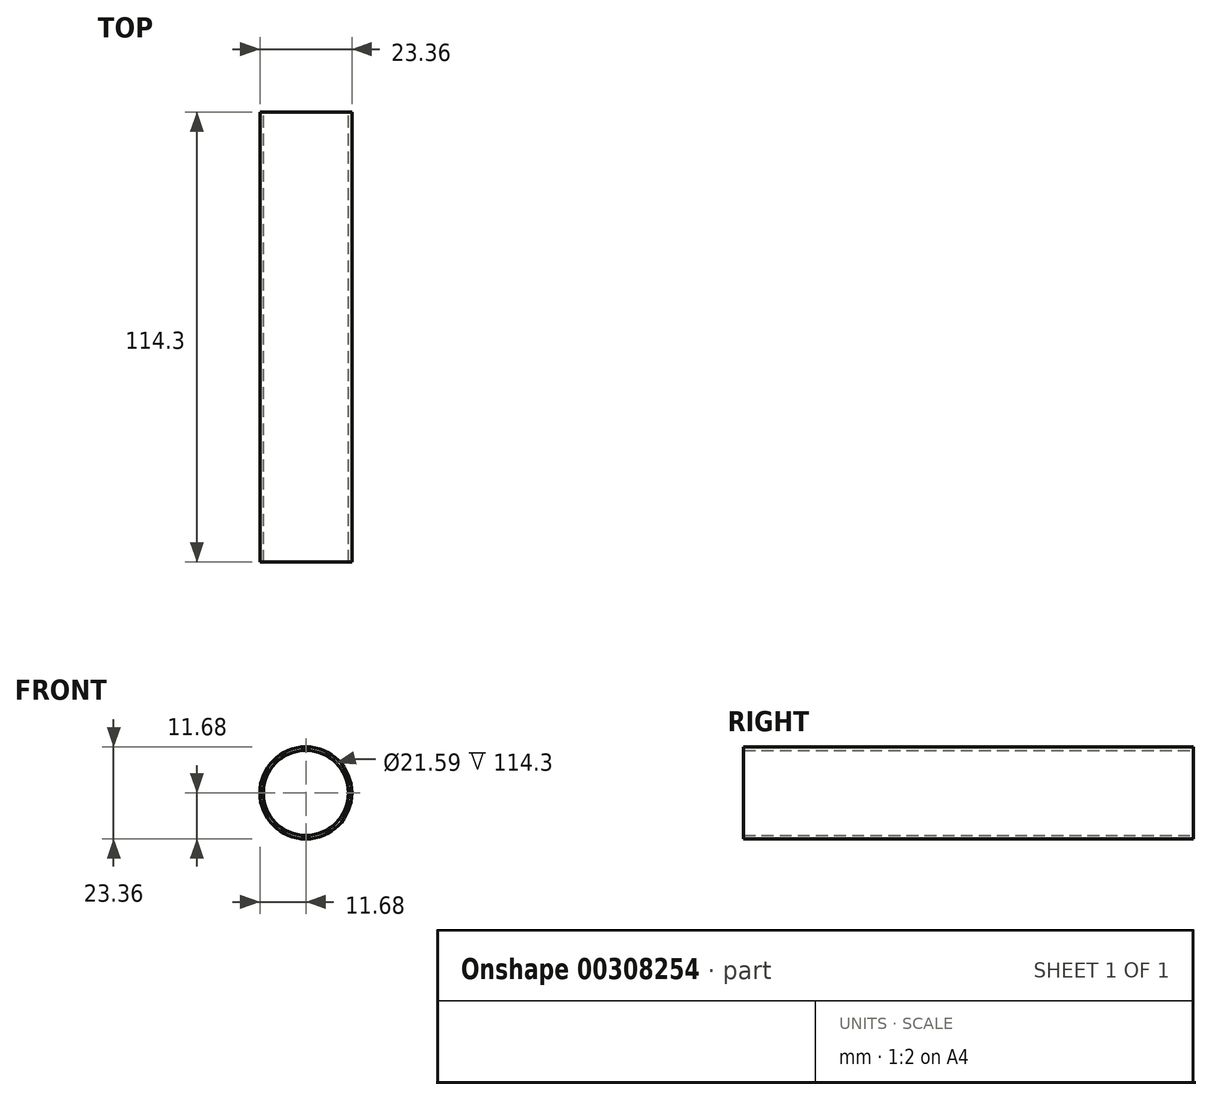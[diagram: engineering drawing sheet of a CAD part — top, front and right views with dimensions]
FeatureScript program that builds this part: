
annotation { "Feature Type Name" : "Feature", "Feature Type Description" : "" }
export const myFeature = defineFeature(function(context is Context, id is Id, definition is map)
    precondition{}
    {
        {
            var Q0;
            Q0=qCreatedBy(makeId("Front.planeOp"),FACE);
            var sketch = newSketch(context, id + "F0", { "sketchPlane" : qUnion([Q0])});
            skCircle(sketch, "E0", {"center": v(0, 0) * mm, "radius": 11.68 * mm});
            skCircle(sketch, "E1", {"center": v(0, 0) * mm, "radius": 10.8 * mm});
            skSolve(sketch);
        }
        {
            var Q0;
            Q0=makeQuery(id+"F0.imprint","IMPRINT",FACE,{"disambiguationData":[TD([[makeQuery(id+"F0.imprint","IMPRINT",EDGE,{"derivedFrom":sQuery(id+"F0.wireOp",EDGE,"E0")}),1.0]])]});
            extrude(context, id + "F1", {"entities" : qUnion([Q0]), "depth" : 114.3 * mm});
        }
    });
